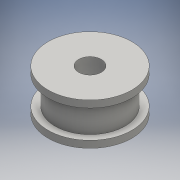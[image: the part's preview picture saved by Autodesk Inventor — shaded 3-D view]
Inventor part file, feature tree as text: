
AUTODESK INVENTOR PART (.ipt)
format: ipt  version: 2016 (Build 200138000, 138)  size: 119,296 bytes
history: native  units: mm
features: sketch x5, extrude x4
ambient origin geometry x8: Origin, YZ Plane, XZ Plane, XY Plane, X Axis, Y Axis, Z Axis, Center Point
bodies: Solid1 (feature_tree)
feature tree (9):
  extrude  "Extrusion1"  Depth=6.5mm
  extrude  "Extrusion2"  Depth=12.0mm
  sketch  "Sketch3"  dims[d5=2.0mm d6=0.0mm d7=6.5mm]
  extrude  "Extrusion3"  Depth=2.0mm
  extrude  "Extrusion4"  Depth=2.0mm TaperAngle=0.0deg
  sketch  "Sketch5"  dims[d11=2.0mm d12=0.0mm]
  sketch  "Sketch1"  dims[d0=20.0mm d1=6.5mm]
  sketch  "Sketch2"  dims[d2=12.0mm d3=0.0mm d4=24.0mm]
  sketch  "Sketch4"  dims[d8=24.0mm d9=2.0mm d10=0.0mm]
